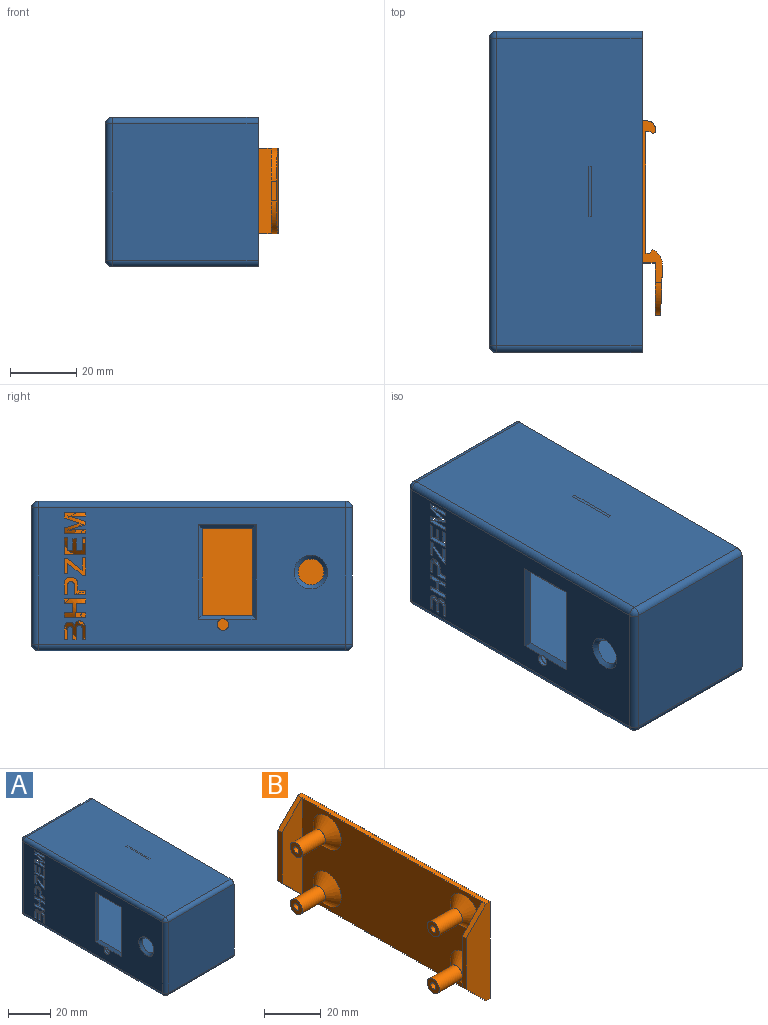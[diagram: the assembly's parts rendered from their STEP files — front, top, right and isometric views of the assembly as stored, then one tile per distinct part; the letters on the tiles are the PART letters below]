
ASSEMBLY  parts=2 mates=1
PART A: 160 faces, bbox 46.2x97.2x45.2 mm
  f0: plane 3.34x1.2mm, normal (0,0,1), area 4mm2, adj f3,f4,f56,f136
  f1: plane 1.2x1.01mm, normal (0,0,1), area 1.2mm2, adj f3,f4,f105,f127
  f2: plane 1.2x1.01mm, normal (0,0,1), area 1.2mm2, adj f3,f4,f119,f126
  f3: plane 94x42mm, normal (1,0,0), area 3347.4mm2, adj f0,f1,f2,f8,f9,f10,f11,f38
  f4: plane 93.2x41.2mm, normal (-1,0,0), area 3122.2mm2, adj f0,f1,f2,f38,f39,f40,f41,f42
  f5: plane 44.2x41.2mm, normal (0,1,0), area 1553mm2, adj f13,f32,f33,f34,f35,f36,f37,f148
  f6: plane 93.2x44.2mm, normal (0,0,-1), area 4119.4mm2, adj f13,f148,f149,f155
  f7: plane 44.2x41.2mm, normal (0,-1,0), area 1821mm2, adj f13,f149,f150,f159
  f8: plane 94x43mm, normal (0,0,-1), area 3800.3mm2, adj f3,f9,f11,f17,f18,f23,f24,f25
  f9: plane 43x42mm, normal (0,1,0), area 1806mm2, adj f3,f8,f10,f17
  f10: plane 94x43mm, normal (0,0,1), area 3805mm2, adj f3,f9,f11,f14,f15,f16,f17,f18
  f11: plane 43x42mm, normal (0,-1,0), area 1538mm2, adj f3,f8,f10,f18,f32,f33,f34,f35
  f12: plane 93.2x44.2mm, normal (0,0,1), area 4119.4mm2, adj f13,f150,f151,f156
  f13: plane 97.2x45.2mm, normal (1,0,0), area 360mm2, adj f5,f6,f7,f12,f19,f20,f21,f22
  f14: plane 15.8x1.5mm, normal (0,-1,0), area 6.7mm2, adj f10,f16,f18,f19,f26,f27,f28
  f15: plane 15.8x1.5mm, normal (0,1,0), area 6.7mm2, adj f10,f16,f17,f19,f26,f27,f28
  f16: plane 15x0.14mm, normal (1,0,0), area 2.2mm2, adj f10,f14,f15,f28
  f17: plane 42.6x39.8mm, normal (1,0,0), area 36.5mm2, adj f8,f9,f10,f15,f19,f20,f21,f24
  f18: plane 42.6x39.8mm, normal (1,0,0), area 36.4mm2, adj f8,f10,f11,f14,f19,f21,f22,f23
  f19: plane 94.6x15.2mm, normal (0,0,1), area 387.2mm2, adj f13,f14,f15,f17,f18,f20,f22,f27
  f20: plane 42.6x2mm, normal (0,1,0), area 85.2mm2, adj f13,f17,f19,f21
  f21: plane 94.6x15.2mm, normal (0,0,-1), area 391.2mm2, adj f13,f17,f18,f20,f22,f23,f24,f29
  f22: plane 42.6x2mm, normal (0,-1,0), area 85.2mm2, adj f13,f18,f19,f21
  f23: plane 15.8x1.5mm, normal (0,-1,0), area 6.7mm2, adj f8,f18,f21,f25,f29,f30,f31
  f24: plane 15.8x1.5mm, normal (0,1,0), area 6.7mm2, adj f8,f17,f21,f25,f29,f30,f31
  f25: plane 15.3x0.14mm, normal (1,0,0), area 2.2mm2, adj f8,f23,f24,f31
  f26: plane 15x0.91mm, normal (0,0,1), area 13.6mm2, adj f14,f15,f27,f28
  f27: plane 15x1.2mm, normal (-1,0,0), area 18mm2, adj f14,f15,f19,f26
  f28: plane 15x1.69mm, normal (0.62,0,0.78), area 32.6mm2, adj f14,f15,f16,f26
  f29: plane 15.3x1.2mm, normal (-1,0,0), area 18.4mm2, adj f21,f23,f24,f30
  f30: plane 15.3x0.91mm, normal (0,0,-1), area 13.9mm2, adj f23,f24,f29,f31
  f31: plane 15.3x1.69mm, normal (0.62,0,-0.78), area 33.2mm2, adj f23,f24,f25,f30
  f32: plane 9.5x1.6mm, normal (1,0,0), area 15.2mm2, adj f5,f11,f33,f37
  f33: plane 8x1.6mm, normal (0,0,1), area 12.8mm2, adj f5,f11,f32,f34
  f34: plane 12.01x1.6mm, normal (1,0,0), area 19.2mm2, adj f5,f11,f33,f35
  f35: plane 16x1.6mm, normal (0,0,-1), area 25.6mm2, adj f5,f11,f34,f36
  f36: plane 21.5x1.6mm, normal (-1,0,0), area 34.4mm2, adj f5,f11,f35,f37
  f37: plane 8x1.6mm, normal (0,0,1), area 12.8mm2, adj f5,f11,f32,f36
  f38: cylinder r=1.75mm len=3.5mm, axis (-1,0,0), area 13.1mm2, adj f3,f4,f143
  f39: plane 2.79x1.2mm, normal (0,0,1), area 3.4mm2, adj f3,f4,f40,f50
  f40: plane 1.36x1.2mm, normal (0,1,0), area 1.6mm2, adj f3,f4,f39,f41
  f41: plane 6.51x1.2mm, normal (0,0,-1), area 7.8mm2, adj f3,f4,f40,f42
  f42: plane 1.36x1.2mm, normal (0,-1,0), area 1.6mm2, adj f3,f4,f41,f43
  f43: plane 2.59x1.2mm, normal (0,0,1), area 3.1mm2, adj f3,f4,f42,f44
  f44: plane 2.84x1.2mm, normal (0,-1,0), area 3.4mm2, adj f3,f4,f43,f45
  f45: plane 2.59x1.2mm, normal (0,0,-1), area 3.1mm2, adj f3,f4,f44,f46
  f46: plane 1.36x1.2mm, normal (0,-1,0), area 1.6mm2, adj f3,f4,f45,f47
  f47: plane 6.51x1.2mm, normal (0,0,1), area 7.8mm2, adj f3,f4,f46,f48
  f48: plane 1.36x1.2mm, normal (0,1,0), area 1.6mm2, adj f3,f4,f47,f49
  f49: plane 2.79x1.2mm, normal (0,0,-1), area 3.4mm2, adj f3,f4,f48,f50
  f50: plane 2.84x1.2mm, normal (0,1,0), area 3.4mm2, adj f3,f4,f39,f49
  f51: extruded ~1.2x1.12mm, area 1.4mm2, adj f3,f4,f52,f60
  f52: extruded ~1.52x1.2mm, area 2mm2, adj f3,f4,f51,f53
  f53: extruded ~1.8x1.2mm, area 2.3mm2, adj f3,f4,f52,f54
  f54: plane 2.93x1.2mm, normal (0,-1,0), area 3.5mm2, adj f3,f4,f53,f55
  f55: plane 1.2x1.06mm, normal (0,0,1), area 1.3mm2, adj f3,f4,f54,f135
  f56: plane 1.36x1.2mm, normal (0,1,0), area 1.6mm2, adj f0,f3,f4,f57
  f57: plane 2.29x1.2mm, normal (0,0,-1), area 2.8mm2, adj f3,f4,f56,f58
  f58: plane 1.62x1.2mm, normal (0,1,0), area 1.9mm2, adj f3,f4,f57,f59
  f59: extruded ~1.27x1.2mm, area 1.6mm2, adj f3,f4,f58,f60
  f60: extruded ~1.2x0.82mm, area 1.4mm2, adj f3,f4,f51,f59
  f61: plane 3.95x1.2mm, normal (0,0,1), area 4.7mm2, adj f3,f4,f62,f81
  f62: plane 1.21x1.2mm, normal (0,1,0), area 1.5mm2, adj f3,f4,f61,f63
  f63: plane 6.51x1.2mm, normal (0,0,-1), area 7.8mm2, adj f3,f4,f62,f64
  f64: plane 1.82x1.2mm, normal (0,-1,0), area 2.2mm2, adj f3,f4,f63,f65
  f65: plane 3.82x1.2mm, normal (0,-0.3,0.95), area 4.8mm2, adj f3,f4,f64,f66
  f66: plane 1.2x1.04mm, normal (0,-0.27,0.96), area 1.3mm2, adj f3,f4,f65,f67
  f67: plane 1.2x0.87mm, normal (0,-0.25,-0.97), area 1.1mm2, adj f3,f4,f66,f68
  f68: plane 1.2x0.35mm, normal (0,-0.28,-0.96), area 0.4mm2, adj f3,f4,f67,f69
  f69: plane 3.64x1.2mm, normal (0,-0.3,-0.95), area 4.6mm2, adj f3,f4,f68,f70
  f70: plane 1.83x1.2mm, normal (0,-1,0), area 2.2mm2, adj f3,f4,f69,f71
  f71: plane 6.51x1.2mm, normal (0,0,1), area 7.8mm2, adj f3,f4,f70,f72
  f72: plane 1.21x1.2mm, normal (0,1,0), area 1.5mm2, adj f3,f4,f71,f73
  f73: plane 3.95x1.2mm, normal (0,0,-1), area 4.7mm2, adj f3,f4,f72,f74
  f74: extruded ~1.42x1.2mm, area 1.7mm2, adj f3,f4,f73,f75
  f75: plane 1.73x1.2mm, normal (0,0.27,0.96), area 2.2mm2, adj f3,f4,f74,f76
  f76: plane 3.63x1.2mm, normal (0,0.31,0.95), area 4.6mm2, adj f3,f4,f75,f77
  f77: plane 1.2x0.97mm, normal (0,1,0), area 1.2mm2, adj f3,f4,f76,f78
  f78: plane 3.63x1.2mm, normal (0,0.31,-0.95), area 4.6mm2, adj f3,f4,f77,f79
  f79: extruded ~1.73x1.2mm, area 2.2mm2, adj f3,f4,f78,f80
  f80: extruded ~1.2x1.15mm, area 1.4mm2, adj f3,f4,f79,f81
  f81: extruded ~1.2x0.27mm, area 0.3mm2, adj f3,f4,f61,f80
  f82: plane 6.51x1.2mm, normal (0,0,1), area 7.8mm2, adj f3,f4,f83,f93
  f83: plane 5.31x1.2mm, normal (0,1,0), area 6.4mm2, adj f3,f4,f82,f84
  f84: plane 1.2x1.06mm, normal (0,0,-1), area 1.3mm2, adj f3,f4,f83,f85
  f85: plane 3.95x1.2mm, normal (0,-1,0), area 4.7mm2, adj f3,f4,f84,f86
  f86: plane 1.71x1.2mm, normal (0,0,-1), area 2.1mm2, adj f3,f4,f85,f87
  f87: plane 3.48x1.2mm, normal (0,1,0), area 4.2mm2, adj f3,f4,f86,f88
  f88: plane 1.2x1.05mm, normal (0,0,-1), area 1.3mm2, adj f3,f4,f87,f89
  f89: plane 3.48x1.2mm, normal (0,-1,0), area 4.2mm2, adj f3,f4,f88,f90
  f90: plane 1.64x1.2mm, normal (0,0,-1), area 2mm2, adj f3,f4,f89,f91
  f91: plane 3.76x1.2mm, normal (0,1,0), area 4.5mm2, adj f3,f4,f90,f92
  f92: plane 1.2x1.05mm, normal (0,0,-1), area 1.3mm2, adj f3,f4,f91,f93
  f93: plane 5.12x1.2mm, normal (0,-1,0), area 6.1mm2, adj f3,f4,f82,f92
  f94: plane 5.23x1.2mm, normal (0,1,0), area 6.3mm2, adj f3,f4,f95,f103
  f95: plane 1.2x1.07mm, normal (0,0,-1), area 1.3mm2, adj f3,f4,f94,f96
  f96: plane 3.71x1.2mm, normal (0,-1,0), area 4.5mm2, adj f3,f4,f95,f97
  f97: plane 4.5x3.52mm, normal (0,0.62,-0.79), area 6.9mm2, adj f3,f4,f96,f98
  f98: plane 1.2x0.95mm, normal (0,0,-1), area 1.1mm2, adj f3,f4,f97,f99
  f99: plane 4.69x1.2mm, normal (0,-1,0), area 5.6mm2, adj f3,f4,f98,f100
  f100: plane 1.2x1.07mm, normal (0,0,1), area 1.3mm2, adj f3,f4,f99,f101
  f101: plane 3.17x1.2mm, normal (0,1,0), area 3.8mm2, adj f3,f4,f100,f102
  f102: plane 4.48x3.52mm, normal (0,-0.62,0.79), area 6.8mm2, adj f3,f4,f101,f103
  f103: plane 1.2x0.97mm, normal (0,0,1), area 1.2mm2, adj f3,f4,f94,f102
  f104: extruded ~1.85x1.2mm, area 2.3mm2, adj f3,f4,f105,f114
  f105: plane 3.26x1.2mm, normal (0,1,0), area 3.9mm2, adj f1,f3,f4,f104
  f106: plane 1.2x1.01mm, normal (0,0,1), area 1.2mm2, adj f3,f4,f107,f120
  f107: plane 2.98x1.2mm, normal (0,-1,0), area 3.6mm2, adj f3,f4,f106,f108
  f108: extruded ~1.81x1.2mm, area 2.3mm2, adj f3,f4,f107,f109
  f109: extruded ~1.22x1.2mm, area 1.7mm2, adj f3,f4,f108,f110
  f110: extruded ~1.2x0.94mm, area 1.2mm2, adj f3,f4,f109,f111
  f111: extruded ~1.2x0.94mm, area 1.3mm2, adj f3,f4,f110,f112
  f112: extruded ~1.2x1.2mm, area 1.6mm2, adj f3,f4,f111,f113
  f113: extruded ~1.2x1.07mm, area 1.4mm2, adj f3,f4,f112,f114
  f114: extruded ~1.37x1.2mm, area 1.9mm2, adj f3,f4,f104,f113
  f115: plane 1.61x0.8mm, normal (0,0,-1), area 1.3mm2, adj f3,f119,f120,f124
  f116: extruded ~1.2x0.62mm, area 0.9mm2, adj f4,f117,f121,f122
  f117: extruded ~1.2x0.6mm, area 0.8mm2, adj f4,f116,f118,f122
  f118: extruded ~1.2x0.84mm, area 1.1mm2, adj f4,f117,f119,f122
  f119: plane 2.93x2mm, normal (0,-1,0), area 4.6mm2, adj f2,f4,f115,f118,f122,f123,f124
  f120: plane 2.92x2mm, normal (0,1,0), area 4.6mm2, adj f4,f106,f115,f121,f122,f123,f124
  f121: extruded ~1.2x0.83mm, area 1mm2, adj f4,f116,f120,f122
  f122: plane 2.66x1.61mm, normal (1,0,0), area 4mm2, adj f116,f117,f118,f119,f120,f121,f123
  f123: plane 1.61x0.8mm, normal (0,0,1), area 1.3mm2, adj f119,f120,f122,f124
  f124: plane 1.61x1.36mm, normal (1,0,0), area 2.2mm2, adj f115,f119,f120,f123
  f125: plane 1.87x0.8mm, normal (0,0,-1), area 1.5mm2, adj f3,f126,f127,f133
  f126: plane 3.09x2mm, normal (0,1,0), area 4.8mm2, adj f2,f4,f125,f130,f131,f132,f133
  f127: plane 3.14x2mm, normal (0,-1,0), area 4.9mm2, adj f1,f4,f125,f128,f131,f132,f133
  f128: extruded ~1.2x0.96mm, area 1.2mm2, adj f4,f127,f129,f131
  f129: extruded ~1.2x0.71mm, area 1mm2, adj f4,f128,f130,f131
  f130: extruded ~1.31x1.2mm, area 2.2mm2, adj f4,f126,f129,f131
  f131: plane 3.04x1.87mm, normal (1,0,0), area 5.3mm2, adj f126,f127,f128,f129,f130,f132
  f132: plane 1.87x0.8mm, normal (0,0,1), area 1.5mm2, adj f126,f127,f131,f133
  f133: plane 1.87x1.36mm, normal (1,0,0), area 2.5mm2, adj f125,f126,f127,f132
  f134: plane 2.11x0.8mm, normal (0,0,-1), area 1.7mm2, adj f3,f135,f136,f142
  f135: plane 2.77x2mm, normal (0,1,0), area 4.4mm2, adj f4,f55,f134,f139,f140,f141,f142
  f136: plane 2.81x2mm, normal (0,-1,0), area 4.5mm2, adj f0,f4,f134,f137,f140,f141,f142
  f137: extruded ~1.2x0.87mm, area 1.1mm2, adj f4,f136,f138,f140
  f138: extruded ~1.2x0.81mm, area 1.1mm2, adj f4,f137,f139,f140
  f139: extruded ~1.21x1.2mm, area 2.2mm2, adj f4,f135,f138,f140
  f140: plane 2.62x2.11mm, normal (1,0,0), area 5.1mm2, adj f135,f136,f137,f138,f139,f141
  f141: plane 2.11x0.8mm, normal (0,0,1), area 1.7mm2, adj f135,f136,f140,f142
  f142: plane 2.11x1.36mm, normal (1,0,0), area 2.9mm2, adj f134,f135,f136,f141
  f143: plane 17.6x1.2mm, normal (-0.71,0,0.71), area 27.6mm2, adj f3,f4,f38,f144,f145
  f144: plane 28.65x1.2mm, normal (-0.71,-0.71,0), area 46.6mm2, adj f3,f4,f143,f146
  f145: plane 28.65x1.2mm, normal (-0.71,0.71,0), area 46.6mm2, adj f3,f4,f143,f146
  f146: plane 17.6x1.2mm, normal (-0.71,0,-0.71), area 27.8mm2, adj f3,f4,f144,f145
  f147: cone r=3.1mm half-angle=45deg, axis (-1,0,0), area 48mm2, adj f3,f4
  f148: cylinder r=2mm len=44.2mm, axis (1,0,0), area 138.9mm2, adj f5,f6,f13,f153
  f149: cylinder r=2mm len=44.2mm, axis (-1,0,0), area 138.9mm2, adj f6,f7,f13,f157
  f150: cylinder r=2mm len=44.2mm, axis (1,0,0), area 138.9mm2, adj f7,f12,f13,f158
  f151: cylinder r=2mm len=44.2mm, axis (-1,0,0), area 138.9mm2, adj f5,f12,f13,f154
  f152: cylinder r=2mm len=41.2mm, axis (0,0,1), area 129.4mm2, adj f4,f5,f153,f154
  f153: sphere r=2mm, area 6.3mm2, adj f148,f152,f155
  f154: sphere r=2mm, area 6.3mm2, adj f151,f152,f156
  f155: cylinder r=2mm len=93.2mm, axis (0,1,0), area 292.8mm2, adj f4,f6,f153,f157
  f156: cylinder r=2mm len=93.2mm, axis (0,-1,0), area 292.8mm2, adj f4,f12,f154,f158
  f157: sphere r=2mm, area 6.3mm2, adj f149,f155,f159
  f158: sphere r=2mm, area 6.3mm2, adj f150,f156,f159
  f159: cylinder r=2mm len=41.2mm, axis (0,0,-1), area 129.4mm2, adj f4,f7,f157,f158
PART B: 54 faces, bbox 23.6x94x42 mm
  f0: plane 90x42mm, normal (-1,0,0), area 3164.2mm2, adj f1,f2,f39,f40,f41,f42,f46,f48
  f1: plane 94x2mm, normal (0,0,-1), area 188mm2, adj f0,f20,f21,f22,f51,f53
  f2: plane 94x2mm, normal (0,0,1), area 188mm2, adj f0,f20,f21,f22,f50,f52
  f3: plane 26x0.74mm, normal (1,0,0), area 19.2mm2, adj f4,f16,f17,f19
  f4: cylinder r=2.4mm len=26mm, axis (0,0,-1), area 98mm2, adj f3,f5,f16,f17
  f5: plane 26x1.54mm, normal (0,1,0), area 39.9mm2, adj f4,f16,f17,f20
  f6: plane 26x3.94mm, normal (0,-1,0), area 102.3mm2, adj f7,f16,f17,f20
  f7: plane 26x15.84mm, normal (-1,0,0), area 368.9mm2, adj f6,f8,f16,f17,f43,f44
  f8: plane 6x1.6mm, normal (0,-1,0), area 9.6mm2, adj f7,f9,f43,f44
  f9: plane 26x15.08mm, normal (1,-0.04,0), area 349.5mm2, adj f8,f16,f17,f43,f44,f45
  f10: plane 26x1.11mm, normal (-0.75,0.66,0), area 38.5mm2, adj f11,f16,f17,f45
  f11: plane 26x1.17mm, normal (0,1,0), area 30.3mm2, adj f10,f12,f16,f17
  f12: plane 36.83x26mm, normal (1,0,0), area 957.7mm2, adj f11,f13,f16,f17
  f13: plane 26x1.3mm, normal (0,-1,0), area 33.8mm2, adj f12,f14,f16,f17
  f14: plane 26x0.62mm, normal (-0.63,-0.78,0), area 20.6mm2, adj f13,f16,f17,f18
  f15: plane 26x0.35mm, normal (0.72,-0.69,0), area 12.5mm2, adj f16,f17,f18,f19
  f16: plane 48.84x6.1mm, normal (0,0,1), area 80.2mm2, adj f3,f4,f5,f6,f7,f9,f10,f11
  f17: plane 48.84x6.1mm, normal (0,0,-1), area 80.2mm2, adj f3,f4,f5,f6,f7,f9,f10,f11
  f18: cylinder r=0.4mm len=26mm, axis (0,0,-1), area 15.4mm2, adj f14,f15,f16,f17
  f19: cylinder r=0.4mm len=26mm, axis (0,0,1), area 8mm2, adj f3,f15,f16,f17
  f20: plane 94x42mm, normal (1,0,0), area 2830mm2, adj f1,f2,f5,f6,f16,f17,f21,f22
  f21: plane 42x12mm, normal (0,-1,0), area 404mm2, adj f1,f2,f20,f47,f52,f53
  f22: plane 42x12mm, normal (0,1,0), area 404mm2, adj f1,f2,f20,f49,f50,f51
  f23: cylinder r=1.3mm len=15.5mm, axis (1,0,0), area 126.6mm2, adj f25,f26
  f24: cylinder r=3mm len=11.5mm, axis (1,0,0), area 216.8mm2, adj f25,f39
  f25: plane 6x6mm, normal (-1,0,0), area 23mm2, adj f23,f24
  f26: plane 2.6x2.6mm, normal (-1,0,0), area 5.3mm2, adj f23
  f27: cylinder r=1.3mm len=15.5mm, axis (1,0,0), area 126.6mm2, adj f29,f30
  f28: cylinder r=3mm len=11.5mm, axis (1,0,0), area 216.8mm2, adj f29,f40
  f29: plane 6x6mm, normal (-1,0,0), area 23mm2, adj f27,f28
  f30: plane 2.6x2.6mm, normal (-1,0,0), area 5.3mm2, adj f27
  f31: cylinder r=1.3mm len=15.5mm, axis (1,0,0), area 126.6mm2, adj f33,f34
  f32: cylinder r=3mm len=11.5mm, axis (1,0,0), area 216.8mm2, adj f33,f42
  f33: plane 6x6mm, normal (-1,0,0), area 23mm2, adj f31,f32
  f34: plane 2.6x2.6mm, normal (-1,0,0), area 5.3mm2, adj f31
  f35: cylinder r=1.3mm len=15.5mm, axis (1,0,0), area 126.6mm2, adj f37,f38
  f36: cylinder r=3mm len=11.5mm, axis (1,0,0), area 216.8mm2, adj f37,f41
  f37: plane 6x6mm, normal (-1,0,0), area 23mm2, adj f35,f36
  f38: plane 2.6x2.6mm, normal (-1,0,0), area 5.3mm2, adj f35
  f39: cone r=3mm half-angle=45deg, axis (1,0,0), area 177.7mm2, adj f0,f24
  f40: cone r=3mm half-angle=45deg, axis (1,0,0), area 177.7mm2, adj f0,f28
  f41: cone r=3mm half-angle=45deg, axis (1,0,0), area 177.7mm2, adj f0,f36
  f42: cone r=3mm half-angle=45deg, axis (1,0,0), area 177.7mm2, adj f0,f32
  f43: cylinder r=10mm len=10mm, axis (1,0,0), area 27.3mm2, adj f7,f8,f9,f17
  f44: cylinder r=10mm len=10mm, axis (-1,0,0), area 27.3mm2, adj f7,f8,f9,f16
  f45: cylinder r=5mm len=26mm, axis (0,0,1), area 153.1mm2, adj f9,f10,f16,f17
  f46: plane 42x10mm, normal (0,1,0), area 320mm2, adj f0,f47,f52,f53
  f47: plane 22x2mm, normal (-1,0,0), area 44mm2, adj f21,f46,f52,f53
  f48: plane 42x10mm, normal (0,-1,0), area 320mm2, adj f0,f49,f50,f51
  f49: plane 22x2mm, normal (-1,0,0), area 44mm2, adj f22,f48,f50,f51
  f50: plane 10x10mm, normal (-0.71,0,0.71), area 28.3mm2, adj f2,f22,f48,f49
  f51: plane 10x10mm, normal (-0.71,0,-0.71), area 28.3mm2, adj f1,f22,f48,f49
  f52: plane 10x10mm, normal (-0.71,0,0.71), area 28.3mm2, adj f2,f21,f46,f47
  f53: plane 10x10mm, normal (-0.71,0,-0.71), area 28.3mm2, adj f1,f21,f46,f47
PLACE A rot(axis=(0,0,1),0deg) t=(52.72,5.22,-11.96)mm
PLACE B rot(axis=(0,0,1),0deg) t=(52.79,5.22,-11.66)mm fixed
MATE slider B.f20 <-> A.f13  axis (1,0,0) through (56.1,5.22,-11.66)mm
